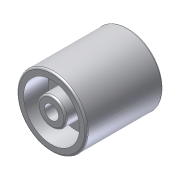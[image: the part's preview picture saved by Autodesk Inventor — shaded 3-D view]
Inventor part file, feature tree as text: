
AUTODESK INVENTOR PART (.ipt)
format: ipt  version: 2012 (Build 160160000, 160)  size: 141,312 bytes
history: native  units: in
note: dims shown in document units (in); Inventor stores cm internally (conversion verified against a paired STEP export)
features: extrude x3, sketch x3, fillet x1
ambient origin geometry x8: Origin, YZ Plane, XZ Plane, XY Plane, X Axis, Y Axis, Z Axis, Center Point
bodies: Solid1 (feature_tree)
feature tree (7):
  extrude  "Extrusion1"  Depth=0.25in
  extrude  "Extrusion2"  Depth=0.25in
  extrude  "Extrusion3"  Depth=0.4375in TaperAngle=0.0deg
  fillet  "Fillet1"  Radius=0.5in
  sketch  "Sketch1"  dims[d0=1.25in d1=0.25in]
  sketch  "Sketch2"  dims[d2=1.375in d3=0.0in d4=0.25in]
  sketch  "Sketch3"  dims[d5=0.5in d6=0.4375in d7=0.0in d8=0.5in d9=0.25in d10=0.4375in d11=0.0in d12=0.0312in]
